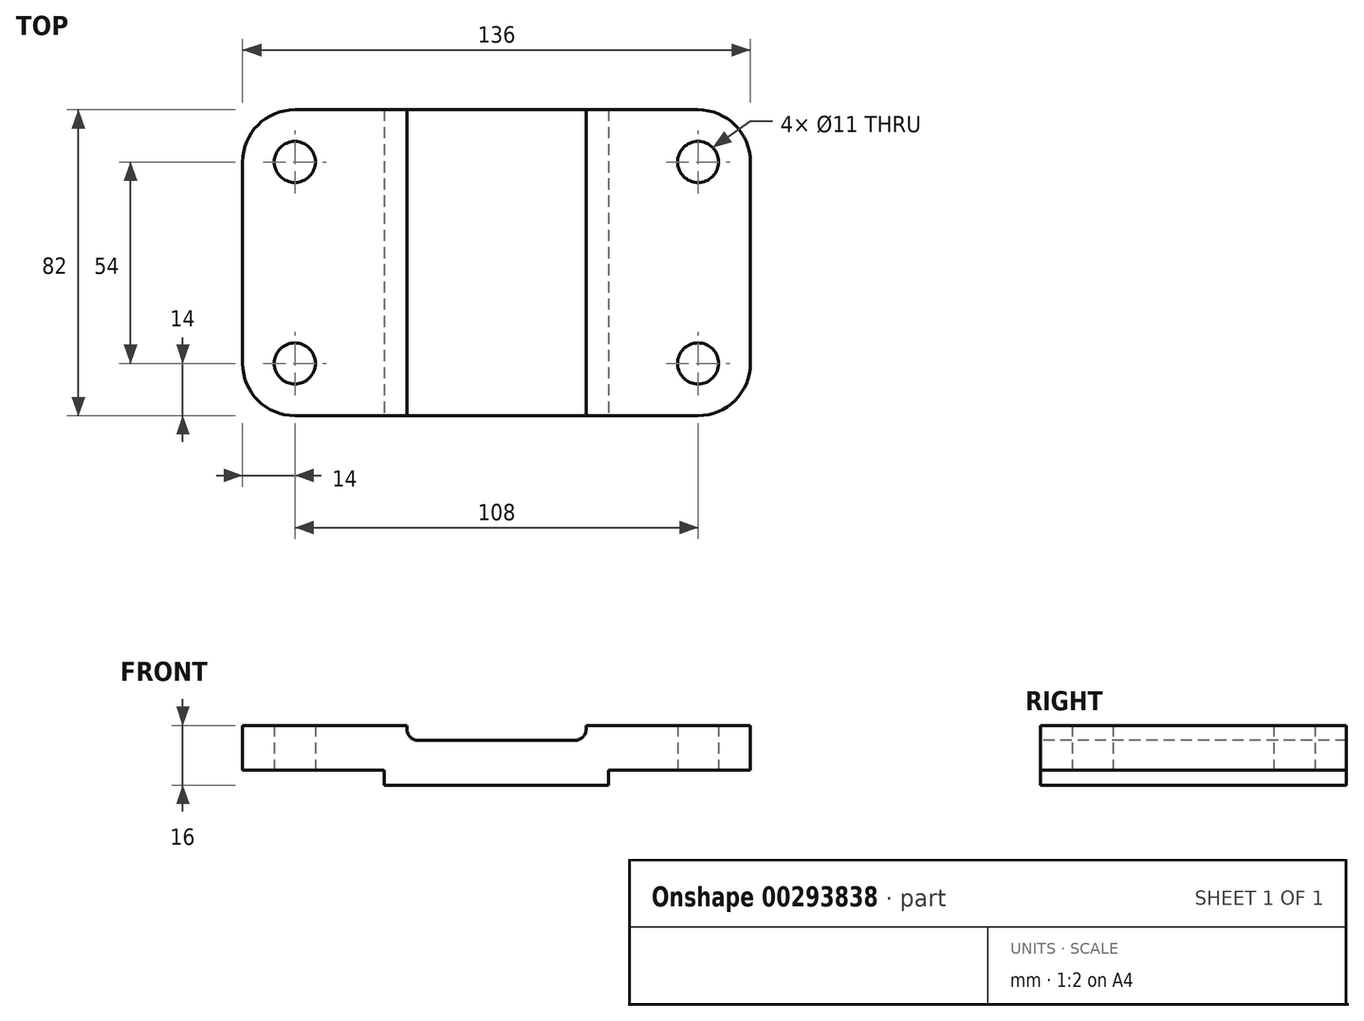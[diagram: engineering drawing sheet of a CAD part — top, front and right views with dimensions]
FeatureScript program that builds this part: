
annotation { "Feature Type Name" : "Feature", "Feature Type Description" : "" }
export const myFeature = defineFeature(function(context is Context, id is Id, definition is map)
    precondition{}
    {
        {
            var Q0;
            Q0=qCreatedBy(makeId("Top.planeOp"),FACE);
            var sketch = newSketch(context, id + "F0", { "sketchPlane" : qUnion([Q0])});
            skLineSegment(sketch, "E0.bottom", {"start": v(14, 0) * mm, "end": v(122, 0) * mm});
            skLineSegment(sketch, "E0.top", {"start": v(14, 82) * mm, "end": v(122, 82) * mm});
            skLineSegment(sketch, "E0.left", {"start": v(0, 14) * mm, "end": v(0, 68) * mm});
            skLineSegment(sketch, "E0.right", {"start": v(136, 14) * mm, "end": v(136, 68) * mm});
            skPoint(sketch, "E1.visualSharp", {"position": v(0, 0) * mm});
            skArc(sketch, "E1.filletArc", {"start": v(0, 14) * mm, "mid": v(4.1, 4.1) * mm, "end": v(14, 0) * mm});
            skPoint(sketch, "E2.visualSharp", {"position": v(0, 82) * mm});
            skArc(sketch, "E2.filletArc", {"start": v(14, 82) * mm, "mid": v(4.1, 77.9) * mm, "end": v(0, 68) * mm});
            skPoint(sketch, "E3.visualSharp", {"position": v(136, 82) * mm});
            skArc(sketch, "E3.filletArc", {"start": v(136, 68) * mm, "mid": v(131.9, 77.9) * mm, "end": v(122, 82) * mm});
            skPoint(sketch, "E4.visualSharp", {"position": v(136, 0) * mm});
            skArc(sketch, "E4.filletArc", {"start": v(122, 0) * mm, "mid": v(131.9, 4.1) * mm, "end": v(136, 14) * mm});
            skCircle(sketch, "E5", {"center": v(14, 68) * mm, "radius": 5.5 * mm});
            skCircle(sketch, "E6", {"center": v(122, 68) * mm, "radius": 5.5 * mm});
            skCircle(sketch, "E7", {"center": v(14, 14) * mm, "radius": 5.5 * mm});
            skCircle(sketch, "E8", {"center": v(122, 14) * mm, "radius": 5.5 * mm});
            skSolve(sketch);
        }
        {
            var Q0;
            Q0 = qSketchRegion(id + "F0", true);
            extrude(context, id + "F1", {"entities" : qUnion([Q0]), "depth" : 16 * mm});
        }
        {
            var Q0;
            Q0=makeQuery(id+"F1.opExtrude","SWEPT_FACE",FACE,{"disambiguationData":[OSD([sQuery(id+"F0.wireOp",EDGE,"E0.bottom")])]});
            var sketch = newSketch(context, id + "F2", { "sketchPlane" : qUnion([Q0])});
            skLineSegment(sketch, "E9.bottom", {"start": v(0, 0) * mm, "end": v(38, 0) * mm});
            skLineSegment(sketch, "E9.top", {"start": v(0, 4) * mm, "end": v(38, 4) * mm});
            skLineSegment(sketch, "E9.left", {"start": v(0, 0) * mm, "end": v(0, 4) * mm});
            skLineSegment(sketch, "E9.right", {"start": v(38, 0) * mm, "end": v(38, 4) * mm});
            skLineSegment(sketch, "E10", {"start": v(68, 0) * mm, "end": v(68, 3.82) * mm, "construction": true});
            skLineSegment(sketch, "E11.MirrorCS", {"start": v(136, 0) * mm, "end": v(98, 0) * mm});
            skLineSegment(sketch, "E12.MirrorCS", {"start": v(136, 4) * mm, "end": v(98, 4) * mm});
            skLineSegment(sketch, "E13.MirrorCS", {"start": v(136, 0) * mm, "end": v(136, 4) * mm});
            skLineSegment(sketch, "E14.MirrorCS", {"start": v(98, 0) * mm, "end": v(98, 4) * mm});
            skLineSegment(sketch, "E15.bottom", {"start": v(68, 16) * mm, "end": v(92, 16) * mm});
            skLineSegment(sketch, "E15.top", {"start": v(68, 12) * mm, "end": v(89, 12) * mm});
            skLineSegment(sketch, "E15.left", {"start": v(68, 16) * mm, "end": v(68, 12) * mm});
            skLineSegment(sketch, "E15.right", {"start": v(92, 16) * mm, "end": v(92, 15) * mm});
            skLineSegment(sketch, "E16.bottom", {"start": v(68, 16) * mm, "end": v(44, 16) * mm});
            skLineSegment(sketch, "E16.top", {"start": v(68, 12) * mm, "end": v(47, 12) * mm});
            skLineSegment(sketch, "E16.right", {"start": v(44, 16) * mm, "end": v(44, 15) * mm});
            skPoint(sketch, "E17.visualSharp", {"position": v(44, 12) * mm});
            skArc(sketch, "E17.filletArc", {"start": v(44, 15) * mm, "mid": v(44.88, 12.88) * mm, "end": v(47, 12) * mm});
            skPoint(sketch, "E18.visualSharp", {"position": v(92, 12) * mm});
            skArc(sketch, "E18.filletArc", {"start": v(89, 12) * mm, "mid": v(91.12, 12.88) * mm, "end": v(92, 15) * mm});
            skSolve(sketch);
        }
        {
            var Q0;
            Q0 = qSketchRegion(id + "F2", true);
            extrude(context, id + "F3", {"entities" : qUnion([Q0]), "operationType" : NewBodyOperationType.REMOVE, "endBound" : BoundingType.THROUGH_ALL, "oppositeDirection" : true, "depth" : 25 * mm});
        }
    });
